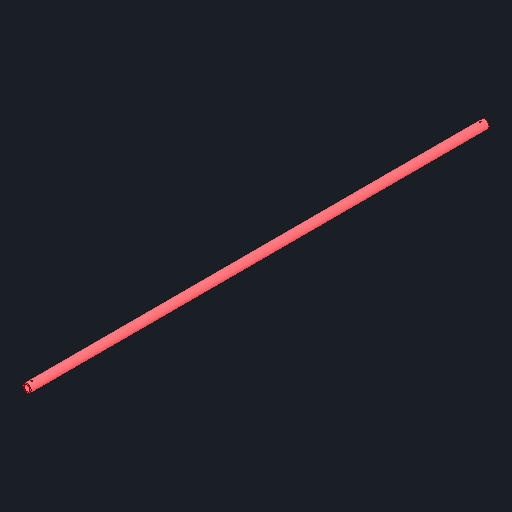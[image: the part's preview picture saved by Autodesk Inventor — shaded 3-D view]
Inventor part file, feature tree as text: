
AUTODESK INVENTOR PART (.ipt)
format: ipt  version: 2024 (Build 280153000, 153)  size: 98,304 bytes
history: native  units: in
note: dims shown in document units (in); Inventor stores cm internally (conversion verified against a paired STEP export)
features: mirror x1
ambient origin geometry x8: Origin, YZ Plane, XZ Plane, XY Plane, X Axis, Y Axis, Z Axis, Center Point
bodies: Solid1 (feature_tree)
feature tree (1):
  mirror  "Mirror1"
